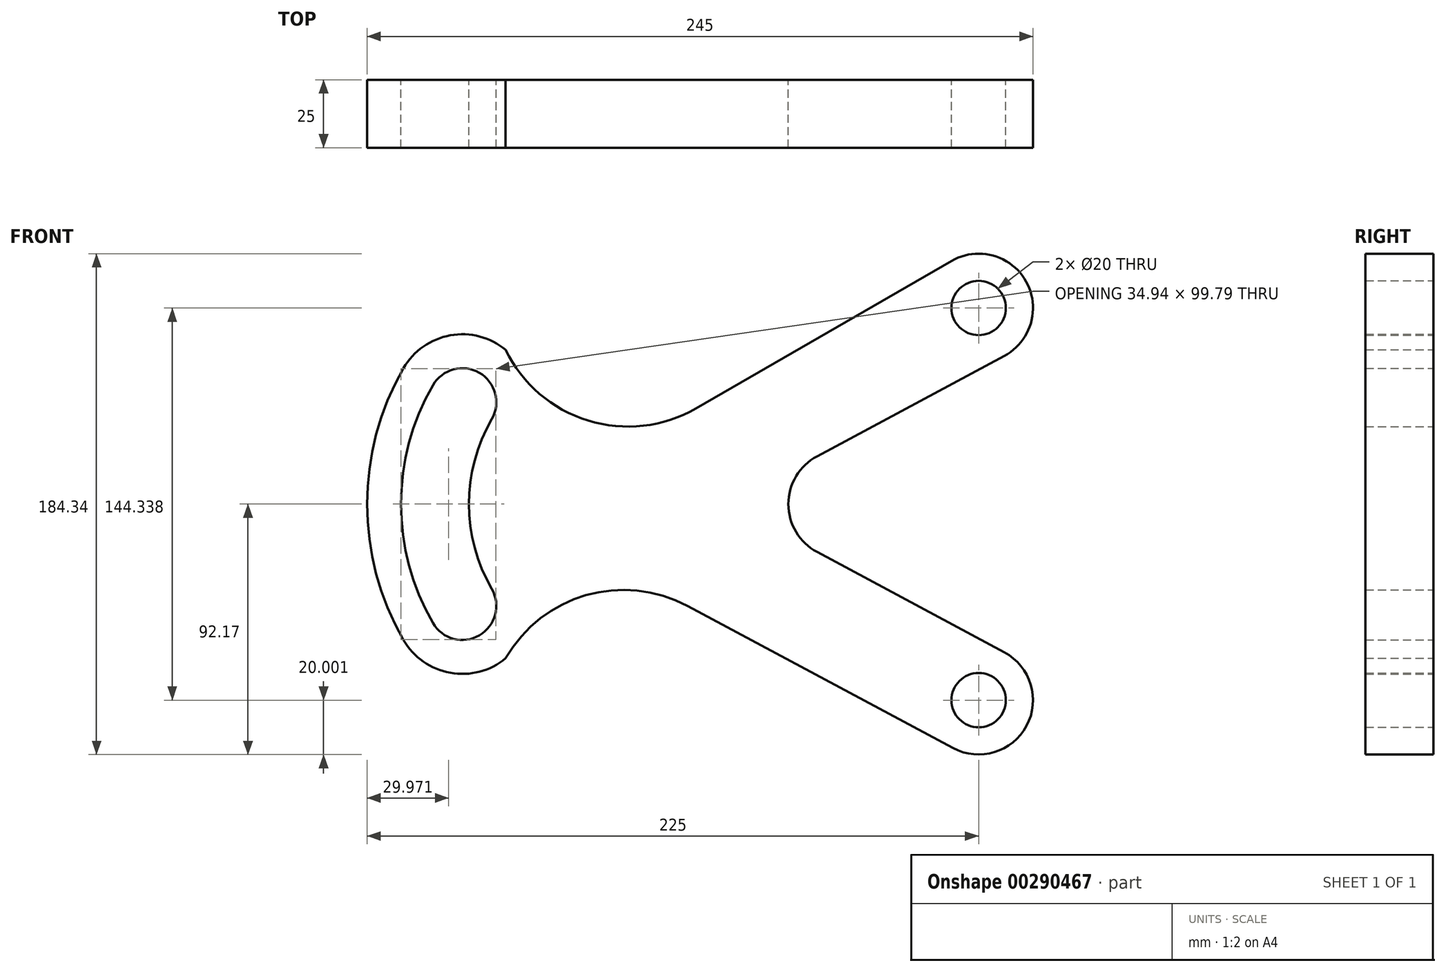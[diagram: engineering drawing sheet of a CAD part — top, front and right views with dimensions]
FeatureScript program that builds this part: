
annotation { "Feature Type Name" : "Feature", "Feature Type Description" : "" }
export const myFeature = defineFeature(function(context is Context, id is Id, definition is map)
    precondition{}
    {
        {
            var Q0;
            Q0=qCreatedBy(makeId("Front.planeOp"),FACE);
            var sketch = newSketch(context, id + "F0", { "sketchPlane" : qUnion([Q0])});
            skLineSegment(sketch, "E0", {"start": v(0, 0) * mm, "end": v(280.88, 162.17) * mm, "construction": true});
            skLineSegment(sketch, "E1", {"start": v(0, 0) * mm, "end": v(-233.05, -134.55) * mm, "construction": true});
            skLineSegment(sketch, "E2", {"start": v(0, 0) * mm, "end": v(-274.73, 158.62) * mm, "construction": true});
            skLineSegment(sketch, "E3", {"start": v(0, 0) * mm, "end": v(262.07, -151.3) * mm, "construction": true});
            skArc(sketch, "E4", {"start": v(134.45, 54.54) * mm, "mid": v(142.48, 81.9) * mm, "end": v(115, 89.49) * mm});
            skCircle(sketch, "E5", {"center": v(125, 72.17) * mm, "radius": 10 * mm});
            skArc(sketch, "E6", {"start": v(115.55, -89.8) * mm, "mid": v(142.63, -81.61) * mm, "end": v(134.45, -54.54) * mm});
            skCircle(sketch, "E7", {"center": v(125, -72.17) * mm, "radius": 10 * mm});
            skArc(sketch, "E8", {"start": v(65.55, 17.63) * mm, "mid": v(55, 0) * mm, "end": v(65.55, -17.63) * mm});
            skLineSegment(sketch, "E9", {"start": v(134.45, 54.54) * mm, "end": v(65.55, 17.63) * mm});
            skLineSegment(sketch, "E10", {"start": v(65.55, -17.63) * mm, "end": v(134.45, -54.54) * mm});
            skLineSegment(sketch, "E11", {"start": v(18, -37.53) * mm, "end": v(115.55, -89.8) * mm});
            skLineSegment(sketch, "E12", {"start": v(21, 35.22) * mm, "end": v(115, 89.49) * mm});
            skLineSegment(sketch, "E13", {"start": v(-184.48, 0) * mm, "end": v(252.95, 0) * mm, "construction": true});
            skArc(sketch, "E14", {"start": v(-57.82, 47.77) * mm, "mid": v(-75, 0) * mm, "end": v(-57.82, -47.77) * mm});
            skArc(sketch, "E15", {"start": v(-64.95, 37.5) * mm, "mid": v(-75, 0) * mm, "end": v(-64.95, -37.5) * mm});
            skArc(sketch, "E16.0.startCap", {"start": v(-75.78, 43.75) * mm, "mid": v(-58.7, 48.33) * mm, "end": v(-54.13, 31.25) * mm});
            skArc(sketch, "E16.0.endCap", {"start": v(-54.13, -31.25) * mm, "mid": v(-58.7, -48.33) * mm, "end": v(-75.78, -43.75) * mm});
            skArc(sketch, "E16.0.left", {"start": v(-54.13, 31.25) * mm, "mid": v(-62.5, 0) * mm, "end": v(-54.13, -31.25) * mm});
            skArc(sketch, "E16.0.right", {"start": v(-75.78, 43.75) * mm, "mid": v(-87.5, 0) * mm, "end": v(-75.78, -43.75) * mm});
            skArc(sketch, "E17.0.startCap", {"start": v(-86.6, 50) * mm, "mid": v(-69.38, 62.1) * mm, "end": v(-49.02, 56.76) * mm});
            skArc(sketch, "E17.0.endCap", {"start": v(-49.02, -56.76) * mm, "mid": v(-69.38, -62.1) * mm, "end": v(-86.6, -50) * mm});
            skArc(sketch, "E17.0.right", {"start": v(-86.6, 50) * mm, "mid": v(-100, 0) * mm, "end": v(-86.6, -50) * mm});
            skArc(sketch, "E18", {"start": v(-49.02, 56.76) * mm, "mid": v(-18.7, 30.73) * mm, "end": v(21, 35.22) * mm});
            skArc(sketch, "E19", {"start": v(18, -37.53) * mm, "mid": v(-19.42, -33.54) * mm, "end": v(-49.02, -56.76) * mm});
            skSolve(sketch);
        }
        {
            var Q0;
            Q0 = qSketchRegion(id + "F0", true);
            extrude(context, id + "F1", {"entities" : qUnion([Q0]), "depth" : 25 * mm});
        }
    });
